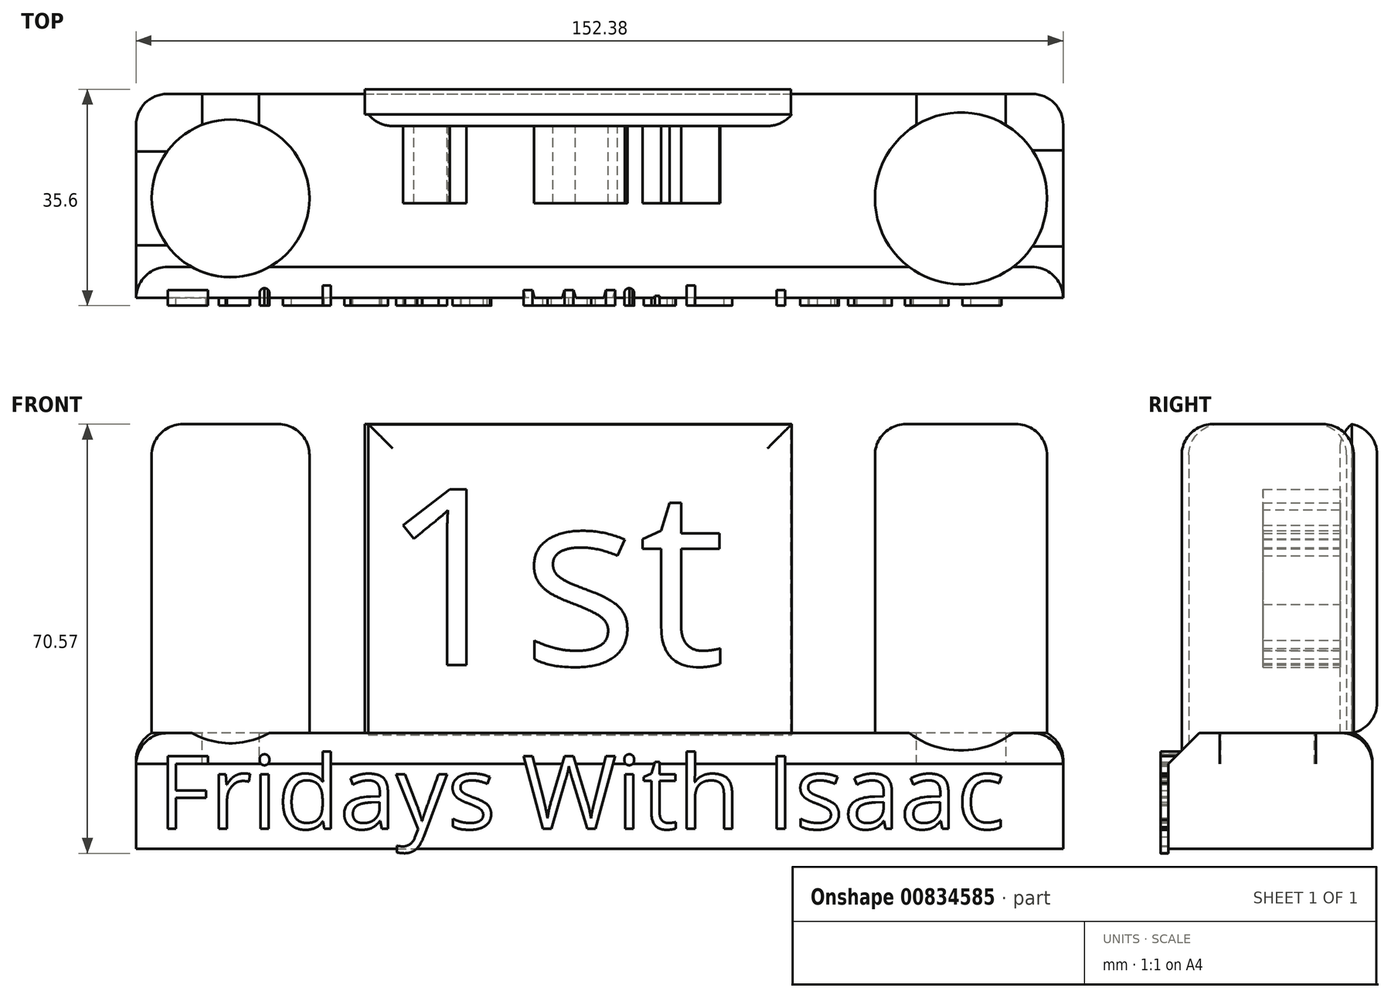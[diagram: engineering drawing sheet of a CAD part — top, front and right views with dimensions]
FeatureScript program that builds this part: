
annotation { "Feature Type Name" : "Feature", "Feature Type Description" : "" }
export const myFeature = defineFeature(function(context is Context, id is Id, definition is map)
    precondition{}
    {
        {
            var Q0;
            Q0=qCreatedBy(makeId("Top.planeOp"),FACE);
            var sketch = newSketch(context, id + "F0", { "sketchPlane" : qUnion([Q0])});
            skLineSegment(sketch, "E0.bottom", {"start": v(-76.18, 33.54) * mm, "end": v(76.2, 33.54) * mm});
            skLineSegment(sketch, "E0.top", {"start": v(-76.18, 0) * mm, "end": v(76.2, 0) * mm});
            skLineSegment(sketch, "E0.left", {"start": v(-76.18, 33.54) * mm, "end": v(-76.18, 0) * mm});
            skLineSegment(sketch, "E0.right", {"start": v(76.2, 33.54) * mm, "end": v(76.2, 0) * mm});
            skSolve(sketch);
        }
        {
            var Q0;
            Q0=makeQuery(id+"F0.imprint","IMPRINT",FACE,{"disambiguationData":[TD([[makeQuery(id+"F0.imprint","IMPRINT",EDGE,{"derivedFrom":sQuery(id+"F0.wireOp",EDGE,"E0.bottom")}),-1.0]])]});
            extrude(context, id + "F1", {"entities" : qUnion([Q0]), "depth" : 19.05 * mm, "offsetDistance" : 25.4 * mm});
        }
        {
            var Q0;
            Q0=makeQuery(id+"F1.opExtrude","SWEPT_FACE",FACE,{"disambiguationData":[OSD([sQuery(id+"F0.wireOp",EDGE,"E0.top")])]});
            var sketch = newSketch(context, id + "F2", { "sketchPlane" : qUnion([Q0])});
            skText(sketch, "E1", { "text": "Fridays With Isaac", "fontName": "OpenSans-Regular.ttf"});
            const initialGuessF2  = {"E1": [-0.07265, 0.0033, 1, 0, 0.01203]};
            skSetInitialGuess(sketch, initialGuessF2);
            skSolve(sketch);
        }
        {
            var Q0;
            Q0 = qSketchRegion(id + "F2", true);
            extrude(context, id + "F3", {"entities" : qUnion([Q0]), "operationType" : NewBodyOperationType.ADD, "depth" : 1.27 * mm, "offsetDistance" : 25.4 * mm});
        }
        {
            var Q0;
            Q0=makeQuery(id+"F1.opExtrude","CAP_FACE",FACE,{"disambiguationData":[OSD([sQuery(id+"F0.wireOp",EDGE,"E0.bottom"),sQuery(id+"F0.wireOp",EDGE,"E0.top"),sQuery(id+"F0.wireOp",EDGE,"E0.left"),sQuery(id+"F0.wireOp",EDGE,"E0.right")])],"isStart":false});
            var sketch = newSketch(context, id + "F4", { "sketchPlane" : qUnion([Q0])});
            skCircle(sketch, "E2", {"center": v(-60.67, 16.36) * mm, "radius": 12.96 * mm});
            skCircle(sketch, "E3", {"center": v(59.4, 16.36) * mm, "radius": 14.14 * mm});
            skSolve(sketch);
        }
        {
            var Q0;
            Q0 = qSketchRegion(id + "F4", true);
            extrude(context, id + "F5", {"entities" : qUnion([Q0]), "operationType" : NewBodyOperationType.ADD, "depth" : 50.8 * mm, "offsetDistance" : 25.4 * mm});
        }
        {
            var Q0;
            Q0=makeQuery(id+"F1.opExtrude","CAP_FACE",FACE,{"disambiguationData":[OSD([sQuery(id+"F0.wireOp",EDGE,"E0.bottom"),sQuery(id+"F0.wireOp",EDGE,"E0.top"),sQuery(id+"F0.wireOp",EDGE,"E0.left"),sQuery(id+"F0.wireOp",EDGE,"E0.right")])],"isStart":false});
            var sketch = newSketch(context, id + "F6", { "sketchPlane" : qUnion([Q0])});
            skLineSegment(sketch, "E4.bottom", {"start": v(-38, 30.17) * mm, "end": v(31.56, 30.17) * mm});
            skLineSegment(sketch, "E4.top", {"start": v(-38, 28.27) * mm, "end": v(31.56, 28.27) * mm});
            skLineSegment(sketch, "E4.left", {"start": v(-38, 30.17) * mm, "end": v(-38, 28.27) * mm});
            skLineSegment(sketch, "E4.right", {"start": v(31.56, 30.17) * mm, "end": v(31.56, 28.27) * mm});
            skSolve(sketch);
        }
        {
            var Q0;
            Q0 = qSketchRegion(id + "F6", true);
            extrude(context, id + "F7", {"entities" : qUnion([Q0]), "operationType" : NewBodyOperationType.ADD, "depth" : 50.8 * mm, "offsetDistance" : 25.4 * mm});
        }
        {
            var Q0;
            Q0=makeQuery(id+"F7.opExtrude","SWEPT_FACE",FACE,{"disambiguationData":[OSD([sQuery(id+"F6.wireOp",EDGE,"E4.top")])]});
            var sketch = newSketch(context, id + "F8", { "sketchPlane" : qUnion([Q0])});
            skText(sketch, "E5", { "text": "1st", "fontName": "OpenSans-Regular.ttf"});
            const initialGuessF8  = {"E5": [-0.03601, 0.03027, 1, 0, 0.02913]};
            skSetInitialGuess(sketch, initialGuessF8);
            skSolve(sketch);
        }
        {
            var Q0;
            Q0 = qSketchRegion(id + "F8", true);
            extrude(context, id + "F9", {"entities" : qUnion([Q0]), "operationType" : NewBodyOperationType.ADD, "depth" : 12.7 * mm, "offsetDistance" : 25.4 * mm});
        }
        {
            var Q0;
            Q0=makeQuery(id+"F5.opExtrude","CAP_FACE",FACE,{"disambiguationData":[OSD([sQuery(id+"F4.wireOp",EDGE,"E2")])],"isStart":false});
            fillet(context, id + "F10", {"entities" : qUnion([Q0]), "radius" : 5.08 * mm, "tangentPropagation" : true, "allowEdgeOverflow" : false});
        }
        {
            var Q0;
            Q0=makeQuery(id+"F5.opExtrude","CAP_FACE",FACE,{"disambiguationData":[OSD([sQuery(id+"F4.wireOp",EDGE,"E3")])],"isStart":false});
            fillet(context, id + "F11", {"entities" : qUnion([Q0]), "radius" : 5.08 * mm, "tangentPropagation" : true, "allowEdgeOverflow" : false});
        }
        {
            var Q0;
            Q0=makeQuery(id+"F7.opExtrude","CAP_EDGE",EDGE,{"disambiguationData":[OSD([sQuery(id+"F6.wireOp",EDGE,"E4.top")])],"isStart":false});
            fillet(context, id + "F12", {"entities" : qUnion([Q0]), "radius" : 5.08 * mm, "tangentPropagation" : true, "allowEdgeOverflow" : false});
        }
        {
            var Q0;
            Q0=makeQuery(id+"F7.opExtrude","SWEPT_EDGE",EDGE,{"disambiguationData":[OSD([sQuery(id+"F6.wireOp",EDGE,"E4.top"),sQuery(id+"F6.wireOp",EDGE,"E4.right")])]});
            fillet(context, id + "F13", {"entities" : qUnion([Q0]), "radius" : 5.08 * mm, "tangentPropagation" : true, "allowEdgeOverflow" : false});
        }
        {
            var Q0;
            Q0=makeQuery(id+"F7.opExtrude","SWEPT_EDGE",EDGE,{"disambiguationData":[OSD([sQuery(id+"F6.wireOp",EDGE,"E4.top"),sQuery(id+"F6.wireOp",EDGE,"E4.left")])]});
            fillet(context, id + "F14", {"entities" : qUnion([Q0]), "radius" : 5.08 * mm, "tangentPropagation" : true, "allowEdgeOverflow" : false});
        }
        {
            var Q0;
            Q0=makeQuery(id+"F1.opExtrude","CAP_EDGE",EDGE,{"disambiguationData":[OSD([sQuery(id+"F0.wireOp",EDGE,"E0.top")])],"isStart":false});
            chamfer(context, id + "F15", {"entities" : qUnion([Q0]), "width" : 5.08 * mm, "tangentPropagation" : true});
        }
        {
            var Q0;
            Q0=makeQuery(id+"F1.opExtrude","CAP_EDGE",EDGE,{"disambiguationData":[OSD([sQuery(id+"F0.wireOp",EDGE,"E0.left")])],"isStart":false});
            fillet(context, id + "F16", {"entities" : qUnion([Q0]), "radius" : 5.08 * mm, "tangentPropagation" : true, "allowEdgeOverflow" : false});
        }
        {
            var Q0;
            Q0=makeQuery(id+"F1.opExtrude","CAP_EDGE",EDGE,{"disambiguationData":[OSD([sQuery(id+"F0.wireOp",EDGE,"E0.right")])],"isStart":false});
            fillet(context, id + "F17", {"entities" : qUnion([Q0]), "radius" : 5.08 * mm, "tangentPropagation" : true, "allowEdgeOverflow" : false});
        }
        {
            var Q0;
            Q0=makeQuery(id+"F1.opExtrude","CAP_EDGE",EDGE,{"disambiguationData":[OSD([sQuery(id+"F0.wireOp",EDGE,"E0.bottom")])],"isStart":false});
            fillet(context, id + "F18", {"entities" : qUnion([Q0]), "radius" : 5.08 * mm, "tangentPropagation" : true, "allowEdgeOverflow" : false});
        }
        {
            var Q0;
            Q0=makeQuery(id+"F18.opFillet","SPLIT",FACE,{"disambiguationData":[OD(2.0)],"derivedFrom":makeQuery(id+"F17.opFillet","SPLIT",FACE,{"disambiguationData":[OD(0.0)],"derivedFrom":makeQuery(id+"F16.opFillet","SPLIT",FACE,{"disambiguationData":[OD(0.0)],"derivedFrom":makeQuery(id+"F1.opExtrude","CAP_FACE",FACE,{"disambiguationData":[OSD([sQuery(id+"F0.wireOp",EDGE,"E0.bottom"),sQuery(id+"F0.wireOp",EDGE,"E0.top"),sQuery(id+"F0.wireOp",EDGE,"E0.left"),sQuery(id+"F0.wireOp",EDGE,"E0.right")])],"isStart":false})})})});
            var sketch = newSketch(context, id + "F19", { "sketchPlane" : qUnion([Q0])});
            skLineSegment(sketch, "E6.bottom", {"start": v(31.47, 30.15) * mm, "end": v(-38.56, 30.15) * mm});
            skLineSegment(sketch, "E6.top", {"start": v(31.47, 34.33) * mm, "end": v(-38.56, 34.33) * mm});
            skLineSegment(sketch, "E6.left", {"start": v(31.47, 30.15) * mm, "end": v(31.47, 34.33) * mm});
            skLineSegment(sketch, "E6.right", {"start": v(-38.56, 30.15) * mm, "end": v(-38.56, 34.33) * mm});
            skSolve(sketch);
        }
        {
            var Q0;
            Q0 = qSketchRegion(id + "F19", true);
            extrude(context, id + "F20", {"entities" : qUnion([Q0]), "operationType" : NewBodyOperationType.ADD, "depth" : 50.8 * mm, "offsetDistance" : 25.4 * mm});
        }
        {
            var Q0;
            Q0=makeQuery(id+"F20.opExtrude","CAP_EDGE",EDGE,{"disambiguationData":[OSD([sQuery(id+"F19.wireOp",EDGE,"E6.top")])],"isStart":false});
            var Q1;
            Q1=makeQuery(id+"F20.opExtrude","CAP_EDGE",EDGE,{"disambiguationData":[OSD([sQuery(id+"F19.wireOp",EDGE,"E6.top")])],"isStart":true});
            fillet(context, id + "F21", {"entities" : qUnion([Q0, Q1]), "radius" : 5.08 * mm, "tangentPropagation" : true, "allowEdgeOverflow" : false});
        }
    });
